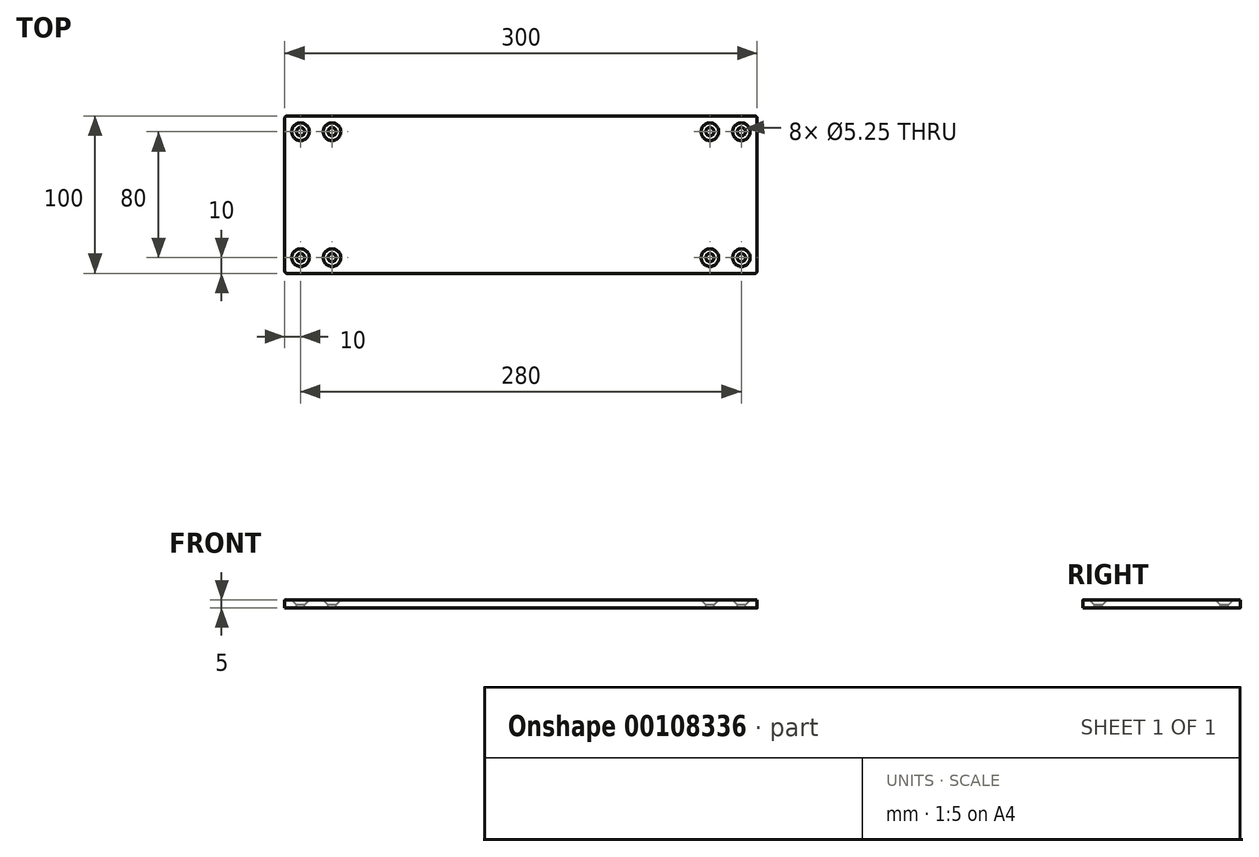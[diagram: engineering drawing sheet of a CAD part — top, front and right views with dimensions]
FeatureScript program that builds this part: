
annotation { "Feature Type Name" : "Feature", "Feature Type Description" : "" }
export const myFeature = defineFeature(function(context is Context, id is Id, definition is map)
    precondition{}
    {
        {
            var Q0;
            Q0=qCreatedBy(makeId("Top.planeOp"),FACE);
            var sketch = newSketch(context, id + "F0", { "sketchPlane" : qUnion([Q0])});
            skLineSegment(sketch, "E0.bottom", {"start": v(0, 0) * mm, "end": v(-300, 0) * mm});
            skLineSegment(sketch, "E0.top", {"start": v(0, 100) * mm, "end": v(-300, 100) * mm});
            skLineSegment(sketch, "E0.left", {"start": v(0, 0) * mm, "end": v(0, 100) * mm});
            skLineSegment(sketch, "E0.right", {"start": v(-300, 0) * mm, "end": v(-300, 100) * mm});
            skLineSegment(sketch, "E1", {"start": v(-300, 50) * mm, "end": v(0, 50) * mm, "construction": true});
            skLineSegment(sketch, "E2", {"start": v(-150, 100) * mm, "end": v(-150, 0) * mm, "construction": true});
            skPoint(sketch, "E3", {"position": v(-290, 10) * mm});
            skPoint(sketch, "E4", {"position": v(-270, 10) * mm});
            skPoint(sketch, "E5.MirrorP", {"position": v(-270, 90) * mm});
            skPoint(sketch, "E6.MirrorP", {"position": v(-290, 90) * mm});
            skPoint(sketch, "E7.MirrorP", {"position": v(-10, 90) * mm});
            skPoint(sketch, "E8.MirrorP", {"position": v(-10, 10) * mm});
            skPoint(sketch, "E9.MirrorP", {"position": v(-30, 10) * mm});
            skPoint(sketch, "E10.MirrorP", {"position": v(-30, 90) * mm});
            skLineSegment(sketch, "E11", {"start": v(-290, 10) * mm, "end": v(-270, 10) * mm});
            skSolve(sketch);
        }
        {
            var Q0;
            Q0=makeQuery(id+"F0.imprint","IMPRINT",FACE,{"disambiguationData":[TD([[makeQuery(id+"F0.imprint","IMPRINT",EDGE,{"derivedFrom":sQuery(id+"F0.wireOp",EDGE,"E0.bottom")}),-1.0]])]});
            extrude(context, id + "F1", {"entities" : qUnion([Q0]), "oppositeDirection" : true, "depth" : 5 * mm});
        }
        {
            var Q0;
            Q0=sQuery(id+"F0.wireOp",VERTEX,"E3");
            var Q1;
            Q1=sQuery(id+"F0.wireOp",VERTEX,"E4");
            var Q2;
            Q2=sQuery(id+"F0.wireOp",VERTEX,"E9.MirrorP");
            var Q3;
            Q3=sQuery(id+"F0.wireOp",VERTEX,"E8.MirrorP");
            var Q4;
            Q4=sQuery(id+"F0.wireOp",VERTEX,"E10.MirrorP");
            var Q5;
            Q5=sQuery(id+"F0.wireOp",VERTEX,"E7.MirrorP");
            var Q6;
            Q6=sQuery(id+"F0.wireOp",VERTEX,"E6.MirrorP");
            var Q7;
            Q7=sQuery(id+"F0.wireOp",VERTEX,"E5.MirrorP");
            var Q8;
            Q8=makeQuery(id+"F1.opExtrude","SWEPT_BODY",BODY,{"disambiguationData":[OSD([sQuery(id+"F0.wireOp",EDGE,"E0.bottom"),sQuery(id+"F0.wireOp",EDGE,"E0.top"),sQuery(id+"F0.wireOp",EDGE,"E0.left"),sQuery(id+"F0.wireOp",EDGE,"E0.right")])]});
            hole(context, id + "F2", {"style" : HoleStyle.C_SINK, "endStyle" : HoleEndStyle.THROUGH, "standardTappedOrClearance" : lookupTablePath({ "standard" : "ISO", "fit" : "Close", "size" : "M5", "type" : "Clearance" }), "standardBlindInLast" : lookupTablePath({ "fit" : "Close", "standard" : "ISO", "size" : "M5", "type" : "Clearance" }), "holeDiameter" : 5.25 * mm, "cSinkDiameter" : 11.2 * mm, "cSinkAngle" : 90 * degree, "locations" : qUnion([Q0, Q1, Q2, Q3, Q4, Q5, Q6, Q7]), "scope" : qUnion([Q8]), "isTappedThrough" : true});
        }
        {
            var Q0;
            Q0=makeQuery(id+"F1.opExtrude","SWEPT_EDGE",EDGE,{"disambiguationData":[OSD([sQuery(id+"F0.wireOp",EDGE,"E0.bottom"),sQuery(id+"F0.wireOp",EDGE,"E0.left")])]});
            var Q1;
            Q1=makeQuery(id+"F1.opExtrude","SWEPT_EDGE",EDGE,{"disambiguationData":[OSD([sQuery(id+"F0.wireOp",EDGE,"E0.top"),sQuery(id+"F0.wireOp",EDGE,"E0.left")])]});
            var Q2;
            Q2=makeQuery(id+"F1.opExtrude","SWEPT_EDGE",EDGE,{"disambiguationData":[OSD([sQuery(id+"F0.wireOp",EDGE,"E0.bottom"),sQuery(id+"F0.wireOp",EDGE,"E0.right")])]});
            var Q3;
            Q3=makeQuery(id+"F1.opExtrude","SWEPT_EDGE",EDGE,{"disambiguationData":[OSD([sQuery(id+"F0.wireOp",EDGE,"E0.top"),sQuery(id+"F0.wireOp",EDGE,"E0.right")])]});
            fillet(context, id + "F3", {"entities" : qUnion([Q0, Q1, Q2, Q3]), "radius" : 1.5 * mm, "tangentPropagation" : true, "allowEdgeOverflow" : false});
        }
    });
